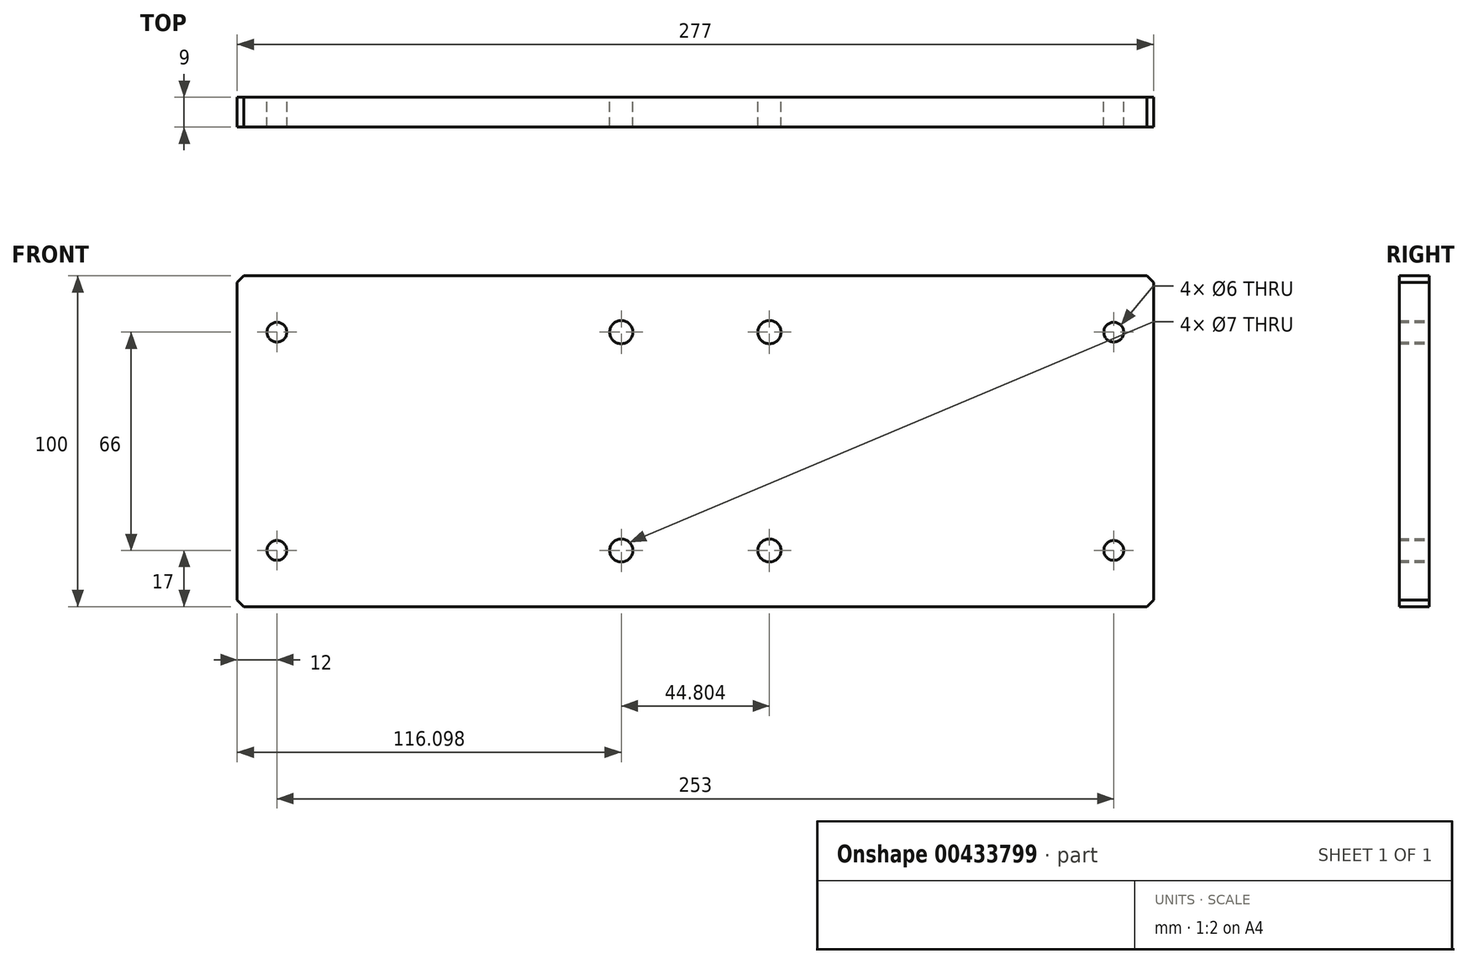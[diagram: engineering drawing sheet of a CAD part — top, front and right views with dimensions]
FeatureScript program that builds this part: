
annotation { "Feature Type Name" : "Feature", "Feature Type Description" : "" }
export const myFeature = defineFeature(function(context is Context, id is Id, definition is map)
    precondition{}
    {
        {
            var Q0;
            Q0=qCreatedBy(makeId("Front.planeOp"),FACE);
            var sketch = newSketch(context, id + "F0", { "sketchPlane" : qUnion([Q0])});
            skLineSegment(sketch, "E0", {"start": v(0, 0) * mm, "end": v(0, 100) * mm});
            skLineSegment(sketch, "E1.0", {"start": v(277, 0) * mm, "end": v(277, 100) * mm});
            skLineSegment(sketch, "E2", {"start": v(0, 0) * mm, "end": v(277, 0) * mm});
            skLineSegment(sketch, "E3.0", {"start": v(0, 100) * mm, "end": v(277, 100) * mm});
            skCircle(sketch, "E4", {"center": v(265, 83) * mm, "radius": 3 * mm});
            skCircle(sketch, "E5", {"center": v(265, 17) * mm, "radius": 3 * mm});
            skCircle(sketch, "E6", {"center": v(160.9, 83) * mm, "radius": 3.5 * mm});
            skCircle(sketch, "E7", {"center": v(160.9, 17) * mm, "radius": 3.5 * mm});
            skCircle(sketch, "E8.MirrorC", {"center": v(116.1, 83) * mm, "radius": 3.5 * mm});
            skCircle(sketch, "E9.MirrorC", {"center": v(116.1, 17) * mm, "radius": 3.5 * mm});
            skCircle(sketch, "E10.MirrorC", {"center": v(12, 17) * mm, "radius": 3 * mm});
            skCircle(sketch, "E11.MirrorC", {"center": v(12, 83) * mm, "radius": 3 * mm});
            skSolve(sketch);
        }
        {
            var Q0;
            Q0 = qSketchRegion(id + "F0", true);
            extrude(context, id + "F1", {"entities" : qUnion([Q0]), "depth" : 9 * mm});
        }
        {
            var Q0;
            Q0=makeQuery(id+"F1.opExtrude","SWEPT_EDGE",EDGE,{"disambiguationData":[OSD([sQuery(id+"F0.wireOp",EDGE,"E1.0"),sQuery(id+"F0.wireOp",EDGE,"E3.0")])]});
            chamfer(context, id + "F2", {"entities" : qUnion([Q0]), "width" : 2 * mm, "tangentPropagation" : true});
        }
        {
            var Q0;
            Q0=makeQuery(id+"F1.opExtrude","SWEPT_EDGE",EDGE,{"disambiguationData":[OSD([sQuery(id+"F0.wireOp",EDGE,"E1.0"),sQuery(id+"F0.wireOp",EDGE,"E2")])]});
            chamfer(context, id + "F3", {"entities" : qUnion([Q0]), "width" : 2 * mm, "tangentPropagation" : true});
        }
        {
            var Q0;
            Q0=makeQuery(id+"F1.opExtrude","SWEPT_EDGE",EDGE,{"disambiguationData":[OSD([sQuery(id+"F0.wireOp",EDGE,"E0"),sQuery(id+"F0.wireOp",EDGE,"E2")])]});
            chamfer(context, id + "F4", {"entities" : qUnion([Q0]), "width" : 2 * mm, "tangentPropagation" : true});
        }
        {
            var Q0;
            Q0=makeQuery(id+"F1.opExtrude","SWEPT_EDGE",EDGE,{"disambiguationData":[OSD([sQuery(id+"F0.wireOp",EDGE,"E0"),sQuery(id+"F0.wireOp",EDGE,"E3.0")])]});
            chamfer(context, id + "F5", {"entities" : qUnion([Q0]), "width" : 2 * mm, "tangentPropagation" : true});
        }
    });
